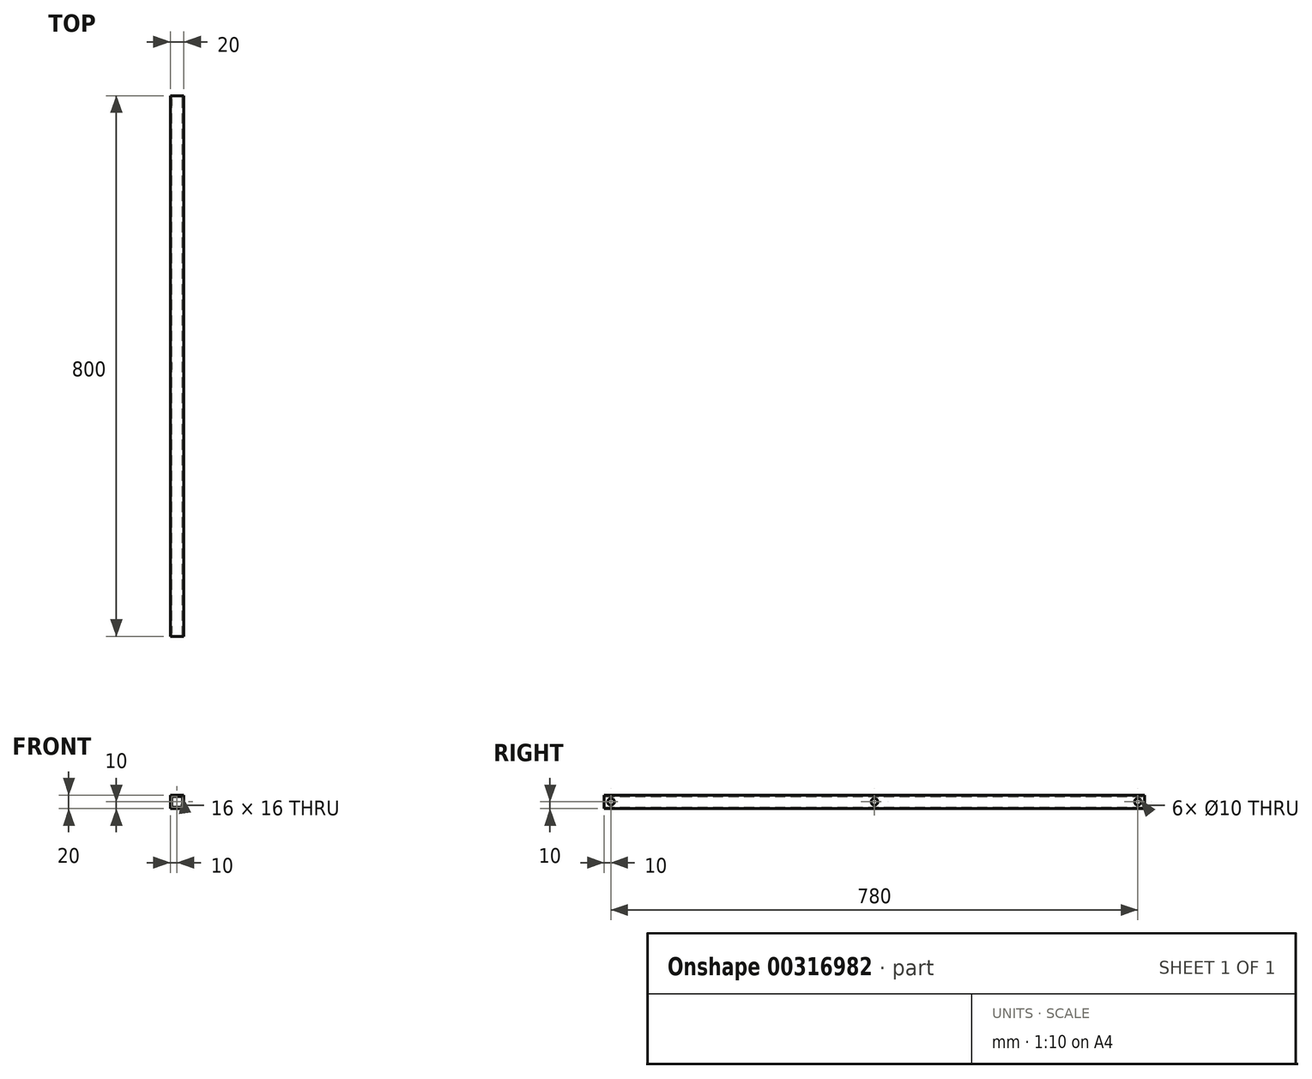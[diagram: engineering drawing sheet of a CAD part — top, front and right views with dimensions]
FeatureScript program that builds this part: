
annotation { "Feature Type Name" : "Feature", "Feature Type Description" : "" }
export const myFeature = defineFeature(function(context is Context, id is Id, definition is map)
    precondition{}
    {
        {
            var Q0;
            Q0=qCreatedBy(makeId("Front.planeOp"),FACE);
            var sketch = newSketch(context, id + "F0", { "sketchPlane" : qUnion([Q0])});
            skLineSegment(sketch, "E0.bottom", {"start": v(0, 20) * mm, "end": v(20, 20) * mm});
            skLineSegment(sketch, "E0.top", {"start": v(0, 0) * mm, "end": v(20, 0) * mm});
            skLineSegment(sketch, "E0.left", {"start": v(0, 20) * mm, "end": v(0, 0) * mm});
            skLineSegment(sketch, "E0.right", {"start": v(20, 20) * mm, "end": v(20, 0) * mm});
            skLineSegment(sketch, "E1.bottom", {"start": v(2, 18) * mm, "end": v(18, 18) * mm});
            skLineSegment(sketch, "E1.top", {"start": v(2, 2) * mm, "end": v(18, 2) * mm});
            skLineSegment(sketch, "E1.left", {"start": v(2, 18) * mm, "end": v(2, 2) * mm});
            skLineSegment(sketch, "E1.right", {"start": v(18, 18) * mm, "end": v(18, 2) * mm});
            skSolve(sketch);
        }
        {
            var Q0;
            Q0=makeQuery(id+"F0.imprint","IMPRINT",FACE,{"disambiguationData":[TD([[makeQuery(id+"F0.imprint","IMPRINT",EDGE,{"derivedFrom":sQuery(id+"F0.wireOp",EDGE,"E0.bottom")}),-1.0]])]});
            extrude(context, id + "F1", {"entities" : qUnion([Q0]), "depth" : 800 * mm});
        }
        {
            var Q0;
            Q0=makeQuery(id+"F1.opExtrude","SWEPT_FACE",FACE,{"disambiguationData":[OSD([sQuery(id+"F0.wireOp",EDGE,"E0.right")])]});
            var sketch = newSketch(context, id + "F2", { "sketchPlane" : qUnion([Q0])});
            skCircle(sketch, "E2", {"center": v(-790, 10) * mm, "radius": 5 * mm});
            skPoint(sketch, "E2.centerSnap0", {"position": v(-800, 10) * mm});
            skCircle(sketch, "E3", {"center": v(-10, 10) * mm, "radius": 5 * mm});
            skPoint(sketch, "E3.centerSnap0", {"position": v(0, 10) * mm});
            skCircle(sketch, "E4", {"center": v(-400, 10) * mm, "radius": 5 * mm});
            skPoint(sketch, "E4.centerSnap0", {"position": v(-400, 0) * mm});
            skSolve(sketch);
        }
        {
            var Q0;
            Q0=makeQuery(id+"F2.imprint","IMPRINT",FACE,{"disambiguationData":[TD([[makeQuery(id+"F2.imprint","IMPRINT",EDGE,{"derivedFrom":sQuery(id+"F2.wireOp",EDGE,"E2")}),1.0]])]});
            var Q1;
            Q1=makeQuery(id+"F2.imprint","IMPRINT",FACE,{"disambiguationData":[TD([[makeQuery(id+"F2.imprint","IMPRINT",EDGE,{"derivedFrom":sQuery(id+"F2.wireOp",EDGE,"E4")}),1.0]])]});
            var Q2;
            Q2=makeQuery(id+"F2.imprint","IMPRINT",FACE,{"disambiguationData":[TD([[makeQuery(id+"F2.imprint","IMPRINT",EDGE,{"derivedFrom":sQuery(id+"F2.wireOp",EDGE,"E3")}),1.0]])]});
            extrude(context, id + "F3", {"entities" : qUnion([Q0, Q1, Q2]), "operationType" : NewBodyOperationType.REMOVE, "endBound" : BoundingType.THROUGH_ALL, "oppositeDirection" : true, "depth" : 25 * mm});
        }
    });
